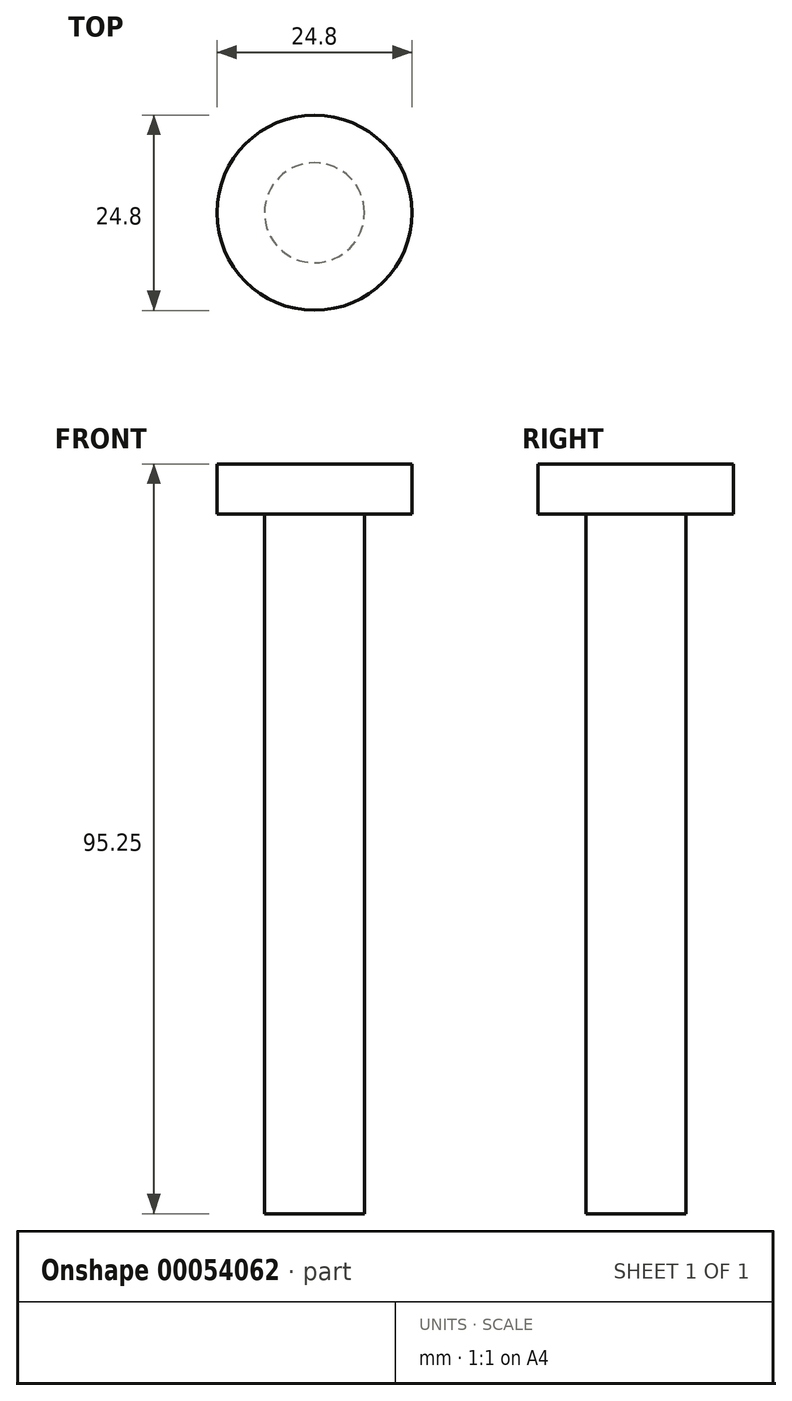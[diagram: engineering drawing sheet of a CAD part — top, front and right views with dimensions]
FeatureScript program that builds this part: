
annotation { "Feature Type Name" : "Feature", "Feature Type Description" : "" }
export const myFeature = defineFeature(function(context is Context, id is Id, definition is map)
    precondition{}
    {
        {
            var Q0;
            Q0=qCreatedBy(makeId("Top.planeOp"),FACE);
            var sketch = newSketch(context, id + "F0", { "sketchPlane" : qUnion([Q0])});
            skCircle(sketch, "E0", {"center": v(0, 0) * mm, "radius": 6.35 * mm});
            skSolve(sketch);
        }
        {
            var Q0;
            Q0 = qSketchRegion(id + "F0", true);
            extrude(context, id + "F1", {"entities" : qUnion([Q0]), "depth" : 88.9 * mm});
        }
        {
            var Q0;
            Q0=makeQuery(id+"F1.opExtrude","CAP_FACE",FACE,{"disambiguationData":[OSD([sQuery(id+"F0.wireOp",EDGE,"E0")])],"isStart":false});
            var sketch = newSketch(context, id + "F2", { "sketchPlane" : qUnion([Q0])});
            skCircle(sketch, "E1", {"center": v(0, 0) * mm, "radius": 12.4 * mm});
            skSolve(sketch);
        }
        {
            var Q0;
            Q0=makeQuery(id+"F2.imprint","IMPRINT",FACE,{"disambiguationData":[TD([[makeQuery(id+"F2.imprint","IMPRINT",EDGE,{"derivedFrom":sQuery(id+"F2.wireOp",EDGE,"E1")}),1.0]])]});
            var Q1;
            Q1=makeQuery(id+"F2.imprint","IMPRINT",FACE,{"disambiguationData":[TD([[makeQuery(id+"F2.imprint","IMPRINT",EDGE,{"derivedFrom":makeQuery(id+"F1.opExtrude","CAP_EDGE",EDGE,{"disambiguationData":[OSD([sQuery(id+"F0.wireOp",EDGE,"E0")])],"isStart":false})}),1.0]])]});
            extrude(context, id + "F3", {"entities" : qUnion([Q0, Q1]), "operationType" : NewBodyOperationType.ADD, "depth" : 6.35 * mm});
        }
    });
